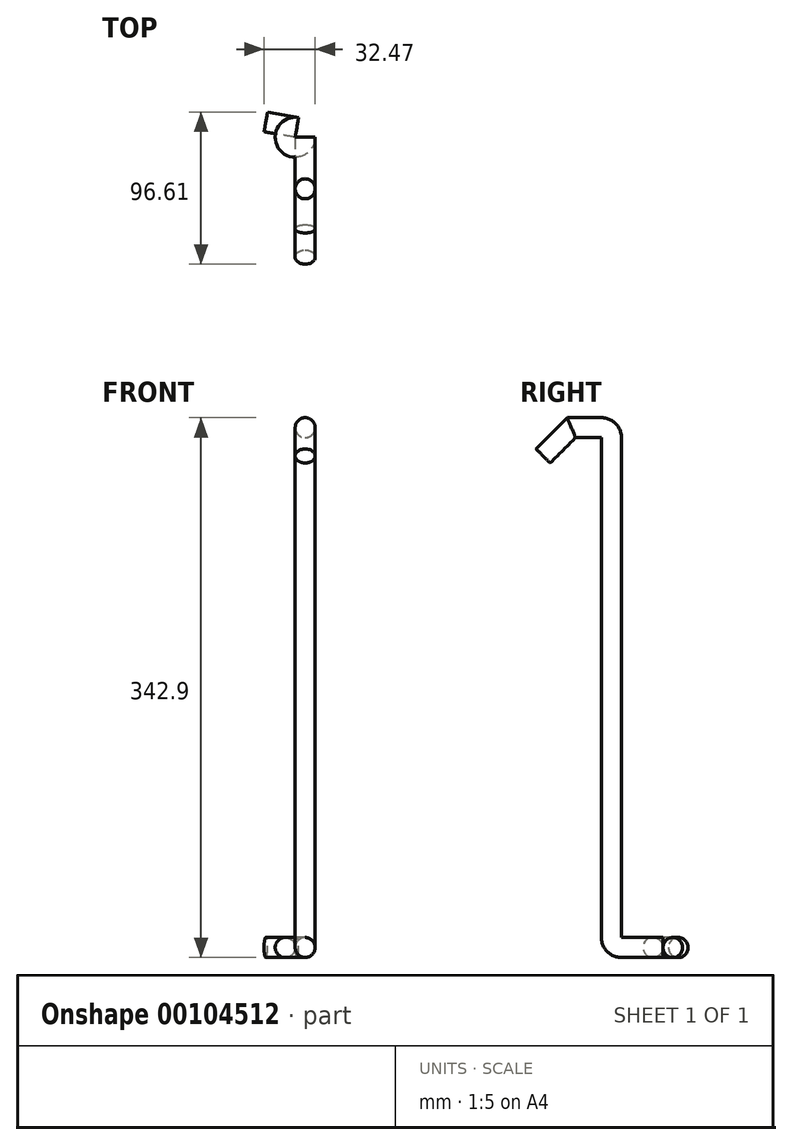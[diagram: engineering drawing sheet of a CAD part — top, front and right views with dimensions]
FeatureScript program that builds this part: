
annotation { "Feature Type Name" : "Feature", "Feature Type Description" : "" }
export const myFeature = defineFeature(function(context is Context, id is Id, definition is map)
    precondition{}
    {
        {
            var Q0;
            Q0=qCreatedBy(makeId("Front.planeOp"),FACE);
            var sketch = newSketch(context, id + "F0", { "sketchPlane" : qUnion([Q0])});
            skCircle(sketch, "E0", {"center": v(0, 0) * mm, "radius": 6.35 * mm});
            skSolve(sketch);
        }
        {
            var Q0;
            Q0=qCreatedBy(makeId("Right.planeOp"),FACE);
            var sketch = newSketch(context, id + "F1", { "sketchPlane" : qUnion([Q0])});
            skPoint(sketch, "E1", {"position": v(-31.75, 330.2) * mm});
            skPoint(sketch, "E2", {"position": v(0, 0) * mm});
            skPoint(sketch, "E3", {"position": v(-31.75, 0) * mm});
            skLineSegment(sketch, "E4", {"start": v(0, 0) * mm, "end": v(-25.4, 0) * mm});
            skLineSegment(sketch, "E5", {"start": v(-31.75, 323.85) * mm, "end": v(-31.75, 6.35) * mm});
            skArc(sketch, "E6.filletArc", {"start": v(-31.75, 6.35) * mm, "mid": v(-29.9, 1.86) * mm, "end": v(-25.4, 0) * mm});
            skPoint(sketch, "E7", {"position": v(-6.35, 330.2) * mm});
            skArc(sketch, "E8.MirrorCS", {"start": v(-38.1, 330.2) * mm, "mid": v(-33.6, 328.34) * mm, "end": v(-31.75, 323.85) * mm});
            skLineSegment(sketch, "E9.MirrorCS", {"start": v(-57.15, 330.2) * mm, "end": v(-38.1, 330.2) * mm});
            skLineSegment(sketch, "E10.MirrorCS", {"start": v(-57.15, 330.2) * mm, "end": v(-75.11, 312.24) * mm});
            skSolve(sketch);
        }
        {
            var Q0;
            Q0=makeQuery(id+"F0.imprint","IMPRINT",FACE,{"disambiguationData":[TD([[makeQuery(id+"F0.imprint","IMPRINT",EDGE,{"derivedFrom":sQuery(id+"F0.wireOp",EDGE,"E0")}),1.0]])]});
            var Q1;
            Q1=sQuery(id+"F1.wireOp",EDGE,"E4");
            var Q2;
            Q2=sQuery(id+"F1.wireOp",EDGE,"E6.filletArc");
            var Q3;
            Q3=sQuery(id+"F1.wireOp",EDGE,"E5");
            var Q4;
            Q4=sQuery(id+"F1.wireOp",EDGE,"4853b471-8b8f-485b-b8a6-606fcc1db4d8.filletArc");
            var Q5;
            Q5=sQuery(id+"F1.wireOp",EDGE,"pOAHB8lk-3QAV-OGAT-kdHc-fd4RSuJAaGUf");
            var Q6;
            Q6=sQuery(id+"F1.wireOp",EDGE,"cdE7xXUD-ZyAN-GIJA-IPYX-7AsicN5qlZLC");
            var Q7;
            Q7=sQuery(id+"F1.wireOp",EDGE,"E8.MirrorCS");
            var Q8;
            Q8=sQuery(id+"F1.wireOp",EDGE,"E9.MirrorCS");
            var Q9;
            Q9=sQuery(id+"F1.wireOp",EDGE,"E10.MirrorCS");
            sweep(context, id + "F2", {"profiles" : qUnion([Q0]), "path" : qUnion([Q1, Q2, Q3, Q4, Q5, Q6, Q7, Q8, Q9])});
        }
        {
            var Q0;
            Q0=qCreatedBy(makeId("Top.planeOp"),FACE);
            var sketch = newSketch(context, id + "F3", { "sketchPlane" : qUnion([Q0])});
            skLineSegment(sketch, "E11", {"start": v(0, 0) * mm, "end": v(0, 1.02) * mm});
            skPoint(sketch, "E12.visualSharp", {"position": v(0, 12.7) * mm});
            skLineSegment(sketch, "E13", {"start": v(-5.25, 7.28) * mm, "end": v(-25.01, 10.76) * mm});
            skPoint(sketch, "E14.visualSharp", {"position": v(0, 6.35) * mm});
            skArc(sketch, "E14.filletArc", {"start": v(0, 1.02) * mm, "mid": v(-1.49, 5.1) * mm, "end": v(-5.25, 7.28) * mm});
            skSolve(sketch);
        }
        {
            var Q0;
            Q0=makeQuery(id+"F2.opSweep","CAP_FACE",FACE,{"disambiguationData":[OSD([sQuery(id+"F0.wireOp",EDGE,"E0"),sQuery(id+"F1.wireOp",VERTEX,"E4.start")])],"isStart":true});
            var Q1;
            Q1=sQuery(id+"F3.wireOp",EDGE,"E11");
            var Q2;
            Q2=sQuery(id+"F3.wireOp",EDGE,"E14.filletArc");
            var Q3;
            Q3=sQuery(id+"F3.wireOp",EDGE,"E13");
            sweep(context, id + "F4", {"operationType" : NewBodyOperationType.ADD, "profiles" : qUnion([Q0]), "path" : qUnion([Q1, Q2, Q3])});
        }
    });
